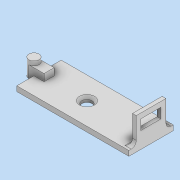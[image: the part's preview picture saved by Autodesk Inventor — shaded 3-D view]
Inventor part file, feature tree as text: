
AUTODESK INVENTOR PART (.ipt)
format: ipt  version: 2022 (Build 260153000, 153)  size: 157,696 bytes
history: native  units: mm
features: sketch x6, extrude x5, fillet x2, hole x1
ambient origin geometry x8: Origin, YZ Plane, XZ Plane, XY Plane, X Axis, Y Axis, Z Axis, Center Point
bodies: Solide1 (feature_tree)
feature tree (14):
  extrude  "Extrusion1"  Depth=42.9mm
  extrude  "Extrusion2"  Depth=17.6mm
  hole  "Perçage2"  [1 undecoded]
  extrude  "Extrusion3"  Depth=4.5mm
  fillet  "Congé1"  Radius=2.0mm
  fillet  "Congé2"  Radius=8.0mm
  extrude  "Extrusion4"  Depth=4.0mm
  extrude  "Extrusion5"  Depth=1.5mm TaperAngle=0.0deg
  sketch  "Esquisse1"
  sketch  "Esquisse2"
  sketch  "Esquisse4"
  sketch  "Esquisse5"
  sketch  "Esquisse6"
  sketch  "Esquisse7"
note: 1 required parameter value undecoded (feature->parameter linkage not recoverable at this tier; creation-order binding heuristic only, values carry confidence <= 0.55)
